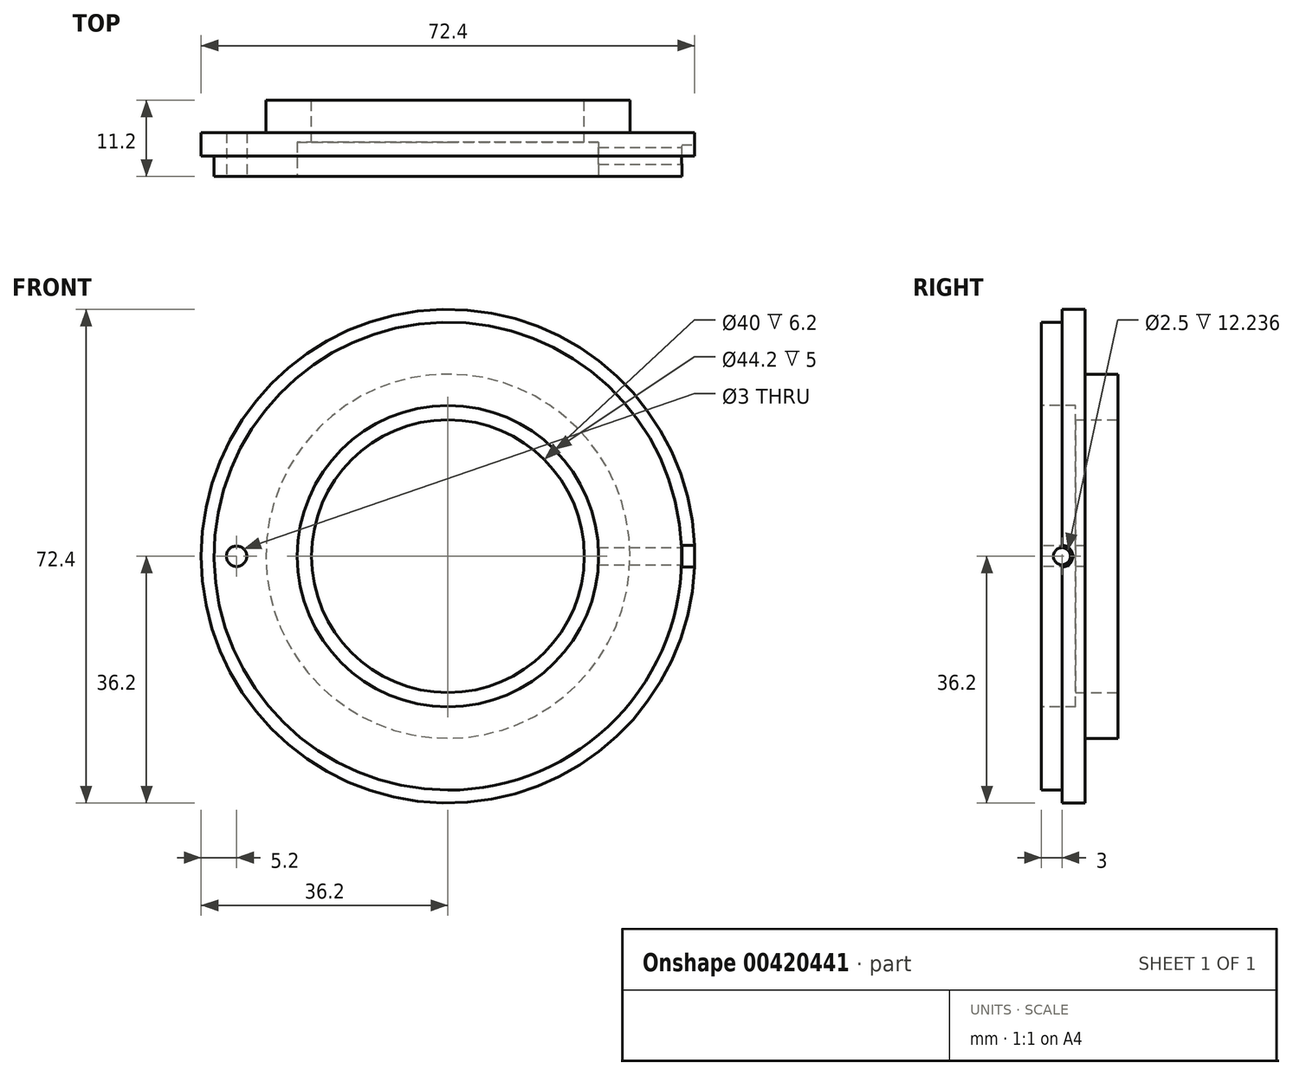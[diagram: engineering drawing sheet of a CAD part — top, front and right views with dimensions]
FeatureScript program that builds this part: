
annotation { "Feature Type Name" : "Feature", "Feature Type Description" : "" }
export const myFeature = defineFeature(function(context is Context, id is Id, definition is map)
    precondition{}
    {
        {
            var Q0;
            Q0=qCreatedBy(makeId("Front.planeOp"),FACE);
            var sketch = newSketch(context, id + "F0", { "sketchPlane" : qUnion([Q0])});
            skCircle(sketch, "E0", {"center": v(0, 0) * mm, "radius": 34.3 * mm});
            skSolve(sketch);
        }
        {
            var Q0;
            Q0 = qSketchRegion(id + "F0", true);
            extrude(context, id + "F1", {"entities" : qUnion([Q0]), "depth" : 3 * mm});
        }
        {
            var Q0;
            Q0=makeQuery(id+"F1.opExtrude","CAP_FACE",FACE,{"disambiguationData":[OSD([sQuery(id+"F0.wireOp",EDGE,"E0")])],"isStart":true});
            var sketch = newSketch(context, id + "F2", { "sketchPlane" : qUnion([Q0])});
            skCircle(sketch, "E1", {"center": v(0, 0) * mm, "radius": 36.2 * mm});
            skSolve(sketch);
        }
        {
            var Q0;
            Q0 = qSketchRegion(id + "F2", true);
            extrude(context, id + "F3", {"entities" : qUnion([Q0]), "operationType" : NewBodyOperationType.ADD, "depth" : 3.4 * mm});
        }
        {
            var Q0;
            Q0=makeQuery(id+"F3.opExtrude","CAP_FACE",FACE,{"disambiguationData":[OSD([sQuery(id+"F2.wireOp",EDGE,"E1")])],"isStart":false});
            var sketch = newSketch(context, id + "F4", { "sketchPlane" : qUnion([Q0])});
            skCircle(sketch, "E2", {"center": v(0, 0) * mm, "radius": 26.7 * mm});
            skSolve(sketch);
        }
        {
            var Q0;
            Q0 = qSketchRegion(id + "F4", true);
            extrude(context, id + "F5", {"entities" : qUnion([Q0]), "operationType" : NewBodyOperationType.ADD, "depth" : 4.8 * mm});
        }
        {
            var Q0;
            Q0=makeQuery(id+"F5.opExtrude","CAP_FACE",FACE,{"disambiguationData":[OSD([sQuery(id+"F4.wireOp",EDGE,"E2")])],"isStart":false});
            var sketch = newSketch(context, id + "F6", { "sketchPlane" : qUnion([Q0])});
            skCircle(sketch, "E3", {"center": v(0, 0) * mm, "radius": 20 * mm});
            skSolve(sketch);
        }
        {
            var Q0;
            Q0 = qSketchRegion(id + "F6", true);
            extrude(context, id + "F7", {"entities" : qUnion([Q0]), "operationType" : NewBodyOperationType.REMOVE, "oppositeDirection" : true, "depth" : 6.2 * mm});
        }
        {
            var Q0;
            Q0=makeQuery(id+"F1.opExtrude","CAP_FACE",FACE,{"disambiguationData":[OSD([sQuery(id+"F0.wireOp",EDGE,"E0")])],"isStart":false});
            var sketch = newSketch(context, id + "F8", { "sketchPlane" : qUnion([Q0])});
            skCircle(sketch, "E4", {"center": v(0, 0) * mm, "radius": 22.1 * mm});
            skSolve(sketch);
        }
        {
            var Q0;
            Q0 = qSketchRegion(id + "F8", true);
            extrude(context, id + "F9", {"entities" : qUnion([Q0]), "operationType" : NewBodyOperationType.REMOVE, "oppositeDirection" : true, "depth" : 5 * mm});
        }
        {
            var Q0;
            Q0=makeQuery(id+"F1.opExtrude","CAP_FACE",FACE,{"disambiguationData":[OSD([sQuery(id+"F0.wireOp",EDGE,"E0")])],"isStart":false});
            var sketch = newSketch(context, id + "F10", { "sketchPlane" : qUnion([Q0])});
            skCircle(sketch, "E5", {"center": v(-31, 0) * mm, "radius": 1.5 * mm});
            skSolve(sketch);
        }
        {
            var Q0;
            Q0 = qSketchRegion(id + "F10", true);
            extrude(context, id + "F11", {"entities" : qUnion([Q0]), "operationType" : NewBodyOperationType.REMOVE, "oppositeDirection" : true, "depth" : 6.4 * mm});
        }
        {
            var Q0;
            Q0=qCreatedBy(makeId("Right.planeOp"),FACE);
            cPlane(context, id + "F12", {"entities" : qUnion([Q0]), "cplaneType" : CPlaneType.OFFSET, "offset" : 36.2 * mm, "width" : 150 * mm, "height" : 150 * mm});
        }
        {
            var Q0;
            Q0=qCreatedBy(id+"F12.planeOp",FACE);
            var sketch = newSketch(context, id + "F13", { "sketchPlane" : qUnion([Q0])});
            skCircle(sketch, "E6", {"center": v(0, 0) * mm, "radius": 1.6 * mm});
            skSolve(sketch);
        }
        {
            var Q0;
            Q0 = qSketchRegion(id + "F13", true);
            extrude(context, id + "F14", {"entities" : qUnion([Q0]), "operationType" : NewBodyOperationType.REMOVE, "oppositeDirection" : true, "depth" : 1.9 * mm});
        }
        {
            var Q0;
            Q0=qCreatedBy(id+"F12.planeOp",FACE);
            var sketch = newSketch(context, id + "F15", { "sketchPlane" : qUnion([Q0])});
            skCircle(sketch, "E7", {"center": v(0, 0) * mm, "radius": 1.25 * mm});
            skSolve(sketch);
        }
        {
            var Q0;
            Q0 = qSketchRegion(id + "F15", true);
            extrude(context, id + "F16", {"entities" : qUnion([Q0]), "operationType" : NewBodyOperationType.REMOVE, "oppositeDirection" : true, "depth" : 15 * mm});
        }
    });
